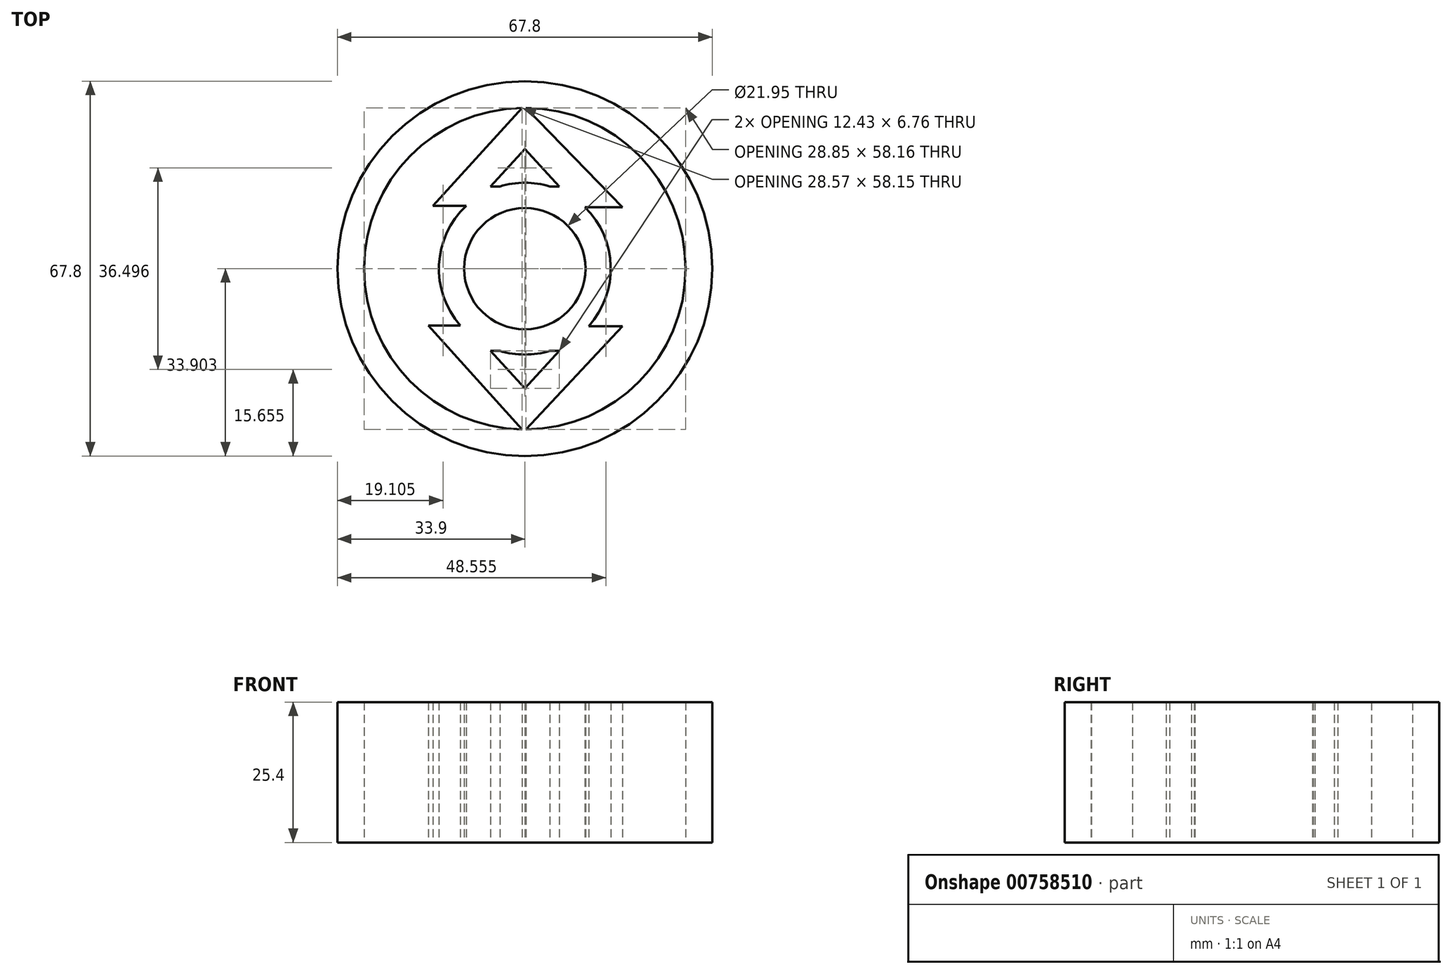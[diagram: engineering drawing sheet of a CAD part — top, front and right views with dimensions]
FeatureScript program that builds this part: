
annotation { "Feature Type Name" : "Feature", "Feature Type Description" : "" }
export const myFeature = defineFeature(function(context is Context, id is Id, definition is map)
    precondition{}
    {
        {
            var Q0;
            Q0=qCreatedBy(makeId("Top.planeOp"),FACE);
            var sketch = newSketch(context, id + "F0", { "sketchPlane" : qUnion([Q0])});
            skCircle(sketch, "E0", {"center": v(35.9, 38.46) * mm, "radius": 33.9 * mm});
            skArc(sketch, "E1", {"start": v(36.13, 9.38) * mm, "mid": v(64.98, 38.46) * mm, "end": v(36.13, 67.54) * mm});
            skArc(sketch, "E2", {"start": v(31.38, 23.6) * mm, "mid": v(35.9, 22.92) * mm, "end": v(40.42, 23.6) * mm});
            skCircle(sketch, "E3", {"center": v(35.9, 38.46) * mm, "radius": 10.98 * mm});
            skLineSegment(sketch, "E4", {"start": v(19.27, 49.86) * mm, "end": v(25.33, 49.86) * mm});
            skLineSegment(sketch, "E5", {"start": v(19.27, 49.86) * mm, "end": v(35.4, 67.54) * mm});
            skLineSegment(sketch, "E6", {"start": v(36.13, 67.54) * mm, "end": v(53.53, 49.54) * mm});
            skLineSegment(sketch, "E7", {"start": v(53.53, 49.54) * mm, "end": v(46.8, 49.54) * mm});
            skLineSegment(sketch, "E8", {"start": v(31.38, 53.33) * mm, "end": v(29.68, 53.33) * mm});
            skLineSegment(sketch, "E9", {"start": v(29.68, 53.33) * mm, "end": v(35.9, 60.1) * mm});
            skLineSegment(sketch, "E10.MirrorCS", {"start": v(42.12, 53.33) * mm, "end": v(35.9, 60.1) * mm});
            skLineSegment(sketch, "E11.MirrorCS", {"start": v(40.42, 53.33) * mm, "end": v(42.12, 53.33) * mm});
            skLineSegment(sketch, "E12.MirrorCS", {"start": v(18.44, 28.18) * mm, "end": v(35.4, 9.39) * mm});
            skLineSegment(sketch, "E13.MirrorCS", {"start": v(36.13, 9.38) * mm, "end": v(53.56, 28.05) * mm});
            skLineSegment(sketch, "E14.MirrorCS", {"start": v(42.12, 23.6) * mm, "end": v(35.9, 16.83) * mm});
            skLineSegment(sketch, "E15.MirrorCS", {"start": v(29.68, 23.6) * mm, "end": v(35.9, 16.83) * mm});
            skLineSegment(sketch, "E16.MirrorCS", {"start": v(31.38, 23.6) * mm, "end": v(29.68, 23.6) * mm});
            skLineSegment(sketch, "E17.MirrorCS", {"start": v(40.42, 23.6) * mm, "end": v(42.12, 23.6) * mm});
            skLineSegment(sketch, "E18", {"start": v(18.44, 28.18) * mm, "end": v(24.25, 28.18) * mm});
            skLineSegment(sketch, "E19", {"start": v(53.56, 28.05) * mm, "end": v(47.43, 28.05) * mm});
            skArc(sketch, "E20.trimOffspring", {"start": v(47.43, 28.05) * mm, "mid": v(51.43, 38.92) * mm, "end": v(46.8, 49.54) * mm});
            skArc(sketch, "E21.trimOffspring", {"start": v(25.33, 49.86) * mm, "mid": v(20.38, 39.24) * mm, "end": v(24.25, 28.18) * mm});
            skArc(sketch, "E22.trimOffspring", {"start": v(40.42, 53.33) * mm, "mid": v(35.9, 54) * mm, "end": v(31.38, 53.33) * mm});
            skArc(sketch, "E23.trimOffspring", {"start": v(35.4, 67.54) * mm, "mid": v(6.82, 38.46) * mm, "end": v(35.4, 9.39) * mm});
            skSolve(sketch);
        }
        {
            var Q0;
            Q0=makeQuery(id+"F0.imprint","IMPRINT",FACE,{"disambiguationData":[TD([[makeQuery(id+"F0.imprint","IMPRINT",EDGE,{"derivedFrom":sQuery(id+"F0.wireOp",EDGE,"E0")}),1.0]])]});
            extrude(context, id + "F1", {"entities" : qUnion([Q0]), "depth" : 25.4 * mm, "offsetDistance" : 25.4 * mm});
        }
    });
